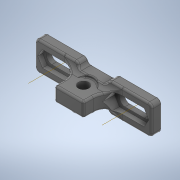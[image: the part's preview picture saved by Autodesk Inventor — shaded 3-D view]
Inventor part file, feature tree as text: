
AUTODESK INVENTOR PART (.ipt)
format: ipt  version: 2020 (Build 240168000, 168)  size: 667,648 bytes
history: native  units: mm
features: fillet x9, sketch x7, extrude x5, projected_geometry x3, hole x2, other x2
ambient origin geometry x8: Origin, YZ Plane, XZ Plane, XY Plane, X Axis, Y Axis, Z Axis, Center Point
bodies: Solid1 (feature_tree)
feature tree (28):
  sketch  "Sketch1"  dims[d0=60.0mm d1=15.0mm]
  extrude  "Extrusion1"  Depth=15.0mm
  extrude  "Extrusion2"  Depth=15.0mm
  sketch  "Sketch2"  dims[d2=7.5mm d4=15.0mm]
  extrude  "Extrusion3"  Depth=17.5mm TaperAngle=0.0deg
  fillet  "Fillet1"  Radius=5.4mm
  fillet  "Fillet2"  Radius=5.4mm
  fillet  "Fillet3"  Radius=10.0mm
  fillet  "Fillet4"  Radius=10.0mm
  fillet  "Fillet5"  [1 undecoded]
  fillet  "Fillet6"  Radius=10.0mm
  extrude  "Extrusion4"  Depth=7.5mm
  extrude  "Extrusion5"  Depth=1.0mm
  fillet  "Fillet7"  Radius=1.0mm
  hole  "Hole1"  [1 undecoded]
  fillet  "Fillet9"  Radius=8.25mm
  other  "Work Axis1"
  other  "Work Axis2"
  hole  "Hole2"  [1 undecoded]
  fillet  "Fillet10"  Radius=7.5mm
  sketch  "Sketch3"  dims[d5=5.0mm d6=0.0mm d7=17.5mm d8=0.0mm d9=5.4mm d10=5.4mm d11=10.0mm d12=10.0mm d13=0.0mm d14=0.0mm d15=10.0mm]
  sketch  "Sketch4"  dims[d16=2.0mm d17=7.5mm]
  sketch  "Sketch5"  dims[d18=3.0mm d19=1.0mm d20=1.0mm]
  sketch  "Sketch6"  dims[d21=1.0mm d22=8.25mm d23=8.25mm]
  sketch  "Sketch7"  dims[d24=10.0mm d25=2.5mm d26=0.0mm d27=0.0mm d28=10.0mm d29=7.5mm d30=2.0mm d31=0.0mm d32=1.0mm d34=5.4mm d35=6.0mm d36=4.0mm d37=2.0mm d38=90.0deg d39=8.0mm d40=20.594885mm d41=0.5mm d42=10.0mm d43=6.0mm d44=4.0mm d45=2.0mm d46=90.0deg d47=8.0mm d48=90.0deg d49=0.5mm]
  projected_geometry  "Project Cut Edges1"
  projected_geometry  "Project Cut Edges2"
  projected_geometry  "Project Cut Edges3"
note: 3 required parameter values undecoded (feature->parameter linkage not recoverable at this tier; creation-order binding heuristic only, values carry confidence <= 0.55)
